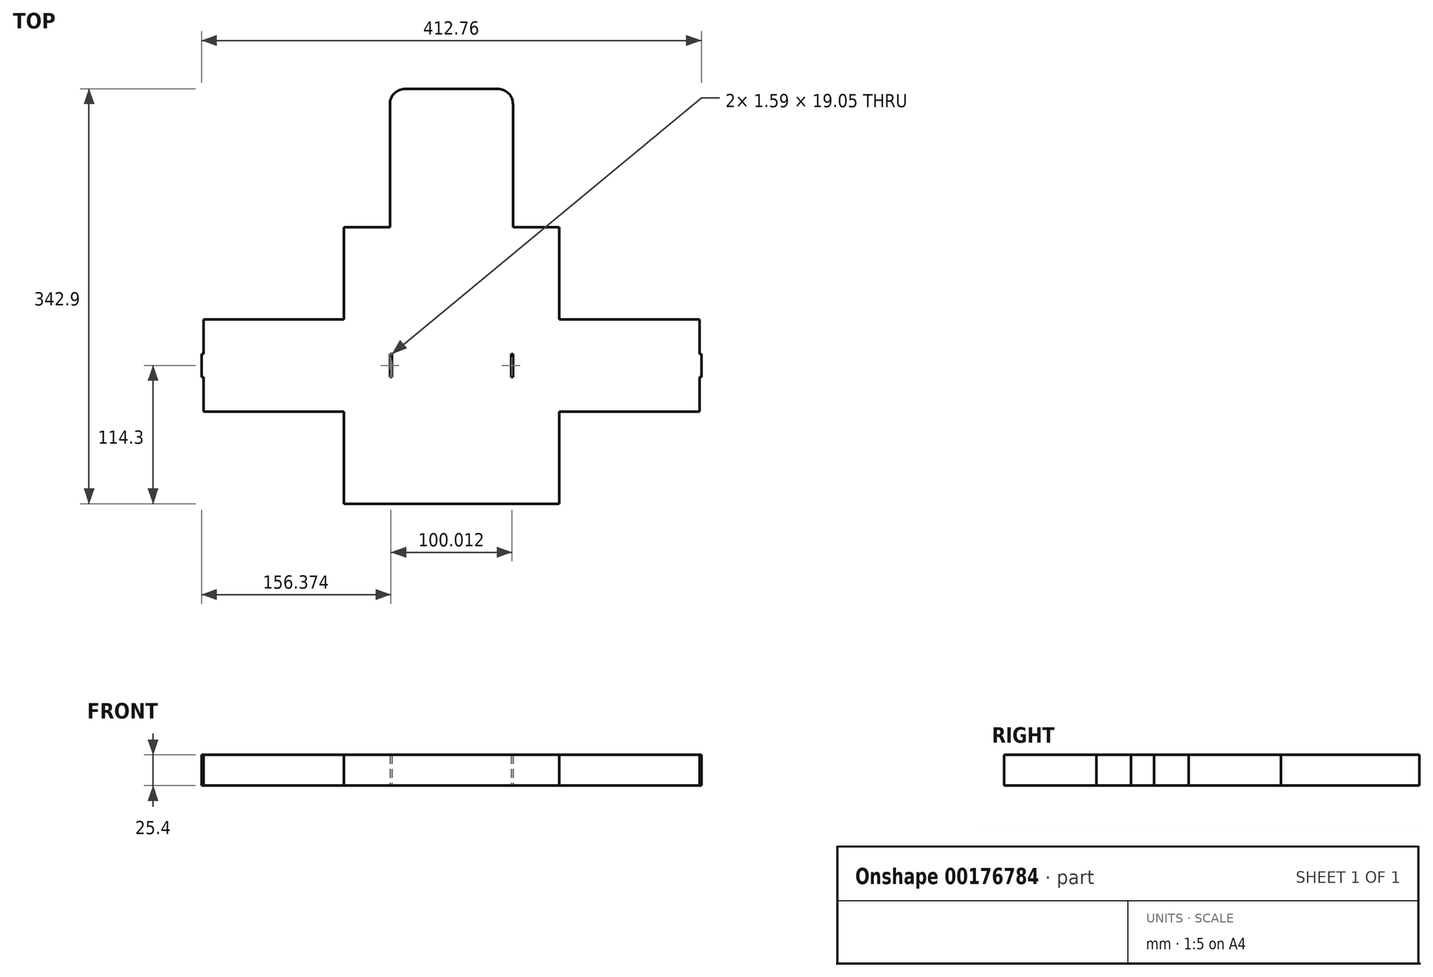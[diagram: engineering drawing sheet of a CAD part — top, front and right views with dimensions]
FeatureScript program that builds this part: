
annotation { "Feature Type Name" : "Feature", "Feature Type Description" : "" }
export const myFeature = defineFeature(function(context is Context, id is Id, definition is map)
    precondition{}
    {
        {
            var Q0;
            Q0=qCreatedBy(makeId("Top.planeOp"),FACE);
            var sketch = newSketch(context, id + "F0", { "sketchPlane" : qUnion([Q0])});
            skLineSegment(sketch, "E0.bottom", {"start": v(50.8, 38.1) * mm, "end": v(-50.8, 38.1) * mm});
            skLineSegment(sketch, "E0.top", {"start": v(50.8, -38.1) * mm, "end": v(-50.8, -38.1) * mm});
            skLineSegment(sketch, "E0.left", {"start": v(50.8, 38.1) * mm, "end": v(50.8, -38.1) * mm});
            skLineSegment(sketch, "E0.right", {"start": v(-50.8, 38.1) * mm, "end": v(-50.8, -38.1) * mm});
            skPoint(sketch, "E0.middle", {"position": v(0, 0) * mm});
            skLineSegment(sketch, "E1", {"start": v(50.8, 38.1) * mm, "end": v(127, 38.1) * mm});
            skLineSegment(sketch, "E2", {"start": v(127, 38.1) * mm, "end": v(127, -38.1) * mm});
            skLineSegment(sketch, "E3", {"start": v(127, -38.1) * mm, "end": v(50.8, -38.1) * mm});
            skLineSegment(sketch, "E4", {"start": v(127, 38.1) * mm, "end": v(128.59, 38.1) * mm});
            skLineSegment(sketch, "E5", {"start": v(128.59, 38.1) * mm, "end": v(128.59, -38.1) * mm});
            skLineSegment(sketch, "E6", {"start": v(128.59, -38.1) * mm, "end": v(127, -38.1) * mm});
            skLineSegment(sketch, "E7", {"start": v(128.59, -38.1) * mm, "end": v(204.79, -38.1) * mm});
            skLineSegment(sketch, "E8", {"start": v(204.79, -38.1) * mm, "end": v(204.79, 38.1) * mm});
            skLineSegment(sketch, "E9", {"start": v(204.79, 38.1) * mm, "end": v(128.59, 38.1) * mm});
            skLineSegment(sketch, "E10", {"start": v(0, 38.1) * mm, "end": v(0, -38.1) * mm, "construction": true});
            skLineSegment(sketch, "E11", {"start": v(-50.8, 0) * mm, "end": v(50.8, 0) * mm, "construction": true});
            skLineSegment(sketch, "E12.MirrorCS", {"start": v(-127, -38.1) * mm, "end": v(-50.8, -38.1) * mm});
            skLineSegment(sketch, "E13.MirrorCS", {"start": v(-50.8, 38.1) * mm, "end": v(-127, 38.1) * mm});
            skLineSegment(sketch, "E14.MirrorCS", {"start": v(-128.59, -38.1) * mm, "end": v(-127, -38.1) * mm});
            skLineSegment(sketch, "E15.MirrorCS", {"start": v(-127, 38.1) * mm, "end": v(-128.59, 38.1) * mm});
            skLineSegment(sketch, "E16.MirrorCS", {"start": v(-204.79, 38.1) * mm, "end": v(-128.59, 38.1) * mm});
            skLineSegment(sketch, "E17.MirrorCS", {"start": v(-128.59, -38.1) * mm, "end": v(-204.79, -38.1) * mm});
            skLineSegment(sketch, "E18.MirrorCS", {"start": v(-204.79, -38.1) * mm, "end": v(-204.79, 38.1) * mm});
            skLineSegment(sketch, "E19.MirrorCS", {"start": v(-127, 38.1) * mm, "end": v(-127, -38.1) * mm});
            skLineSegment(sketch, "E20.MirrorCS", {"start": v(-128.59, 38.1) * mm, "end": v(-128.59, -38.1) * mm});
            skLineSegment(sketch, "E21", {"start": v(-50.8, -38.1) * mm, "end": v(-50.8, -114.3) * mm});
            skLineSegment(sketch, "E22", {"start": v(-50.8, -114.3) * mm, "end": v(50.8, -114.3) * mm});
            skLineSegment(sketch, "E23", {"start": v(50.8, -114.3) * mm, "end": v(50.8, -38.1) * mm});
            skLineSegment(sketch, "E24", {"start": v(-50.8, 38.1) * mm, "end": v(-50.8, 114.3) * mm});
            skLineSegment(sketch, "E25", {"start": v(-50.8, 114.3) * mm, "end": v(50.8, 114.3) * mm});
            skLineSegment(sketch, "E26", {"start": v(50.8, 114.3) * mm, "end": v(50.8, 38.1) * mm});
            skLineSegment(sketch, "E27", {"start": v(50.8, 114.3) * mm, "end": v(50.8, 190.5) * mm});
            skLineSegment(sketch, "E28", {"start": v(50.8, 190.5) * mm, "end": v(-50.8, 190.5) * mm});
            skLineSegment(sketch, "E29", {"start": v(-50.8, 190.5) * mm, "end": v(-50.8, 114.3) * mm});
            skLineSegment(sketch, "E30", {"start": v(-50.8, 190.5) * mm, "end": v(-50.8, 215.9) * mm});
            skLineSegment(sketch, "E31", {"start": v(-38.1, 228.6) * mm, "end": v(38.1, 228.6) * mm});
            skLineSegment(sketch, "E32", {"start": v(50.8, 215.9) * mm, "end": v(50.8, 190.5) * mm});
            skPoint(sketch, "E33.visualSharp", {"position": v(-50.8, 228.6) * mm});
            skArc(sketch, "E33.filletArc", {"start": v(-38.1, 228.6) * mm, "mid": v(-47.08, 224.88) * mm, "end": v(-50.8, 215.9) * mm});
            skPoint(sketch, "E34.visualSharp", {"position": v(50.8, 228.6) * mm});
            skArc(sketch, "E34.filletArc", {"start": v(50.8, 215.9) * mm, "mid": v(47.08, 224.88) * mm, "end": v(38.1, 228.6) * mm});
            skLineSegment(sketch, "E35", {"start": v(-204.79, 9.53) * mm, "end": v(-206.38, 9.53) * mm});
            skLineSegment(sketch, "E36", {"start": v(-206.38, 9.53) * mm, "end": v(-206.38, -9.53) * mm});
            skLineSegment(sketch, "E37", {"start": v(-206.38, -9.53) * mm, "end": v(-204.79, -9.53) * mm});
            skPoint(sketch, "E38", {"position": v(-206.38, 0) * mm});
            skLineSegment(sketch, "E39.bottom", {"start": v(-50.8, 9.53) * mm, "end": v(-49.21, 9.53) * mm});
            skLineSegment(sketch, "E39.top", {"start": v(-50.8, -9.53) * mm, "end": v(-49.21, -9.53) * mm});
            skLineSegment(sketch, "E39.left", {"start": v(-50.8, 9.53) * mm, "end": v(-50.8, -9.53) * mm});
            skLineSegment(sketch, "E39.right", {"start": v(-49.21, 9.53) * mm, "end": v(-49.21, -9.53) * mm});
            skLineSegment(sketch, "E40.MirrorCS", {"start": v(206.38, -9.53) * mm, "end": v(204.79, -9.53) * mm});
            skLineSegment(sketch, "E41.MirrorCS", {"start": v(206.38, 9.53) * mm, "end": v(206.38, -9.53) * mm});
            skLineSegment(sketch, "E42.MirrorCS", {"start": v(204.79, 9.52) * mm, "end": v(206.38, 9.52) * mm});
            skLineSegment(sketch, "E43.MirrorCS", {"start": v(50.8, 9.52) * mm, "end": v(50.8, -9.53) * mm});
            skLineSegment(sketch, "E44.MirrorCS", {"start": v(50.8, 9.52) * mm, "end": v(49.21, 9.52) * mm});
            skLineSegment(sketch, "E45.MirrorCS", {"start": v(50.8, -9.53) * mm, "end": v(49.21, -9.53) * mm});
            skLineSegment(sketch, "E46.MirrorCS", {"start": v(49.21, 9.53) * mm, "end": v(49.21, -9.53) * mm});
            skLineSegment(sketch, "E47", {"start": v(-50.8, -114.3) * mm, "end": v(-88.9, -114.3) * mm});
            skLineSegment(sketch, "E48", {"start": v(-88.9, -114.3) * mm, "end": v(-88.9, -38.1) * mm});
            skLineSegment(sketch, "E49.MirrorCS", {"start": v(50.8, -114.3) * mm, "end": v(88.9, -114.3) * mm});
            skLineSegment(sketch, "E50.MirrorCS", {"start": v(88.9, -114.3) * mm, "end": v(88.9, -38.1) * mm});
            skLineSegment(sketch, "E51.MirrorCS", {"start": v(-88.9, 114.3) * mm, "end": v(-88.9, 38.1) * mm});
            skLineSegment(sketch, "E52.MirrorCS", {"start": v(-50.8, 114.3) * mm, "end": v(-88.9, 114.3) * mm});
            skLineSegment(sketch, "E53.MirrorCS", {"start": v(88.9, 114.3) * mm, "end": v(88.9, 38.1) * mm});
            skLineSegment(sketch, "E54.MirrorCS", {"start": v(50.8, 114.3) * mm, "end": v(88.9, 114.3) * mm});
            skSolve(sketch);
        }
        {
            var Q0;
            Q0 = qSketchRegion(id + "F0", true);
            var Q1;
            {var subQ6=sQuery(id+"F0.wireOp",EDGE,"E0.bottom");Q1=makeQuery(id+"F0.imprint","IMPRINT",FACE,{"disambiguationData":[TD([[makeQuery(id+"F0.imprint","IMPRINT",EDGE,{"derivedFrom":subQ6}),1.0]])]});}
            extrude(context, id + "F1", {"entities" : qUnion([Q0, Q1]), "depth" : 25.4 * mm});
        }
    });
